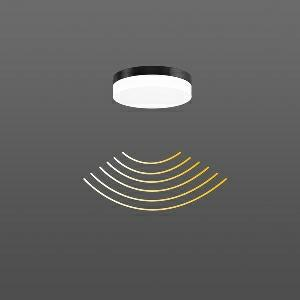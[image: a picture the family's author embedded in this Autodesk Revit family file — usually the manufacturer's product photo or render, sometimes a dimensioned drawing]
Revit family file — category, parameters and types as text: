
# Revit family: flat_slim_round_312135_0031_191_2a42
name_source: partatom
category: Lighting Fixtures
units: mm (PartAtom-declared; Revit-internal decimal feet)

## family parameters
Cut with Voids When Loaded = No
Host = Face
Light Source = No
Part Type = Normal
Room Calculation Point = No
Round Connector Dimension = Use Diameter
Shared = No

## types (1)
- FLAT SLIM round (1 x LED Modul 830, 1150 lm, 3000)
    Apparent Load = 13 VA
    CIE Flux Codes = 43 74 92 91 100
    Color Rendering = 80
    Color Temperature = 3000
    Default Elevation = 1800 mm
    Height = 63 mm
    Lamp = 1 x LED Modul 830
    Lamp Light Flux = 1150 lm
    Lamp count = 1
    Length = 230 mm
    Lifetime = 50000 h
    Luminous efficacy = 88 lm/W
    Manufacturer = RZB
    ModVariant = No
    Model = 312135.0031.191
    Mounting Place = Ceiling, Wall
    Mounting Type = Surface mounted
    Number of Poles = 1
    OnlyDefault = Yes
    Power Factor = 1
    Product Name = FLAT SLIM round
    Product group = Surface mounted ceiling and wall luminaires
    ProductGroupID = 305
    Protection Class = Protection class I
    Protection Degree = IP 65
    RLX_Detail_Level = 1
    RLX_Emergency_Light_Flux = 0 lm
    RLX_Emergency_Type = 0
    RLX_Emergency_Type_DB = No
    RlxData = <blob elided: 34049 chars, md5=c4f45f62>
    Socket = socket
    Standby Power = 0 W
    System Light Flux = 1150 lm
    System Power = 13 W
    Type Comments = Product without accessories
    Type Image = 312132.0031.19.jpg
    URL = http://relux.com
    VarID = ---
    Voltage = 230 V
    Voltage Range = 220-240 V
    Weight = 0.00 kg
    Width = 0 mm  [stored 0 ft]

note: [stored X ft] marks values corroborated as IEEE doubles in the binary element streams (Revit-internal decimal feet)

## geometry (parser evidence)
native form markers: Blend x4, Sweep x11
no freeform markers — native parametric forms only
